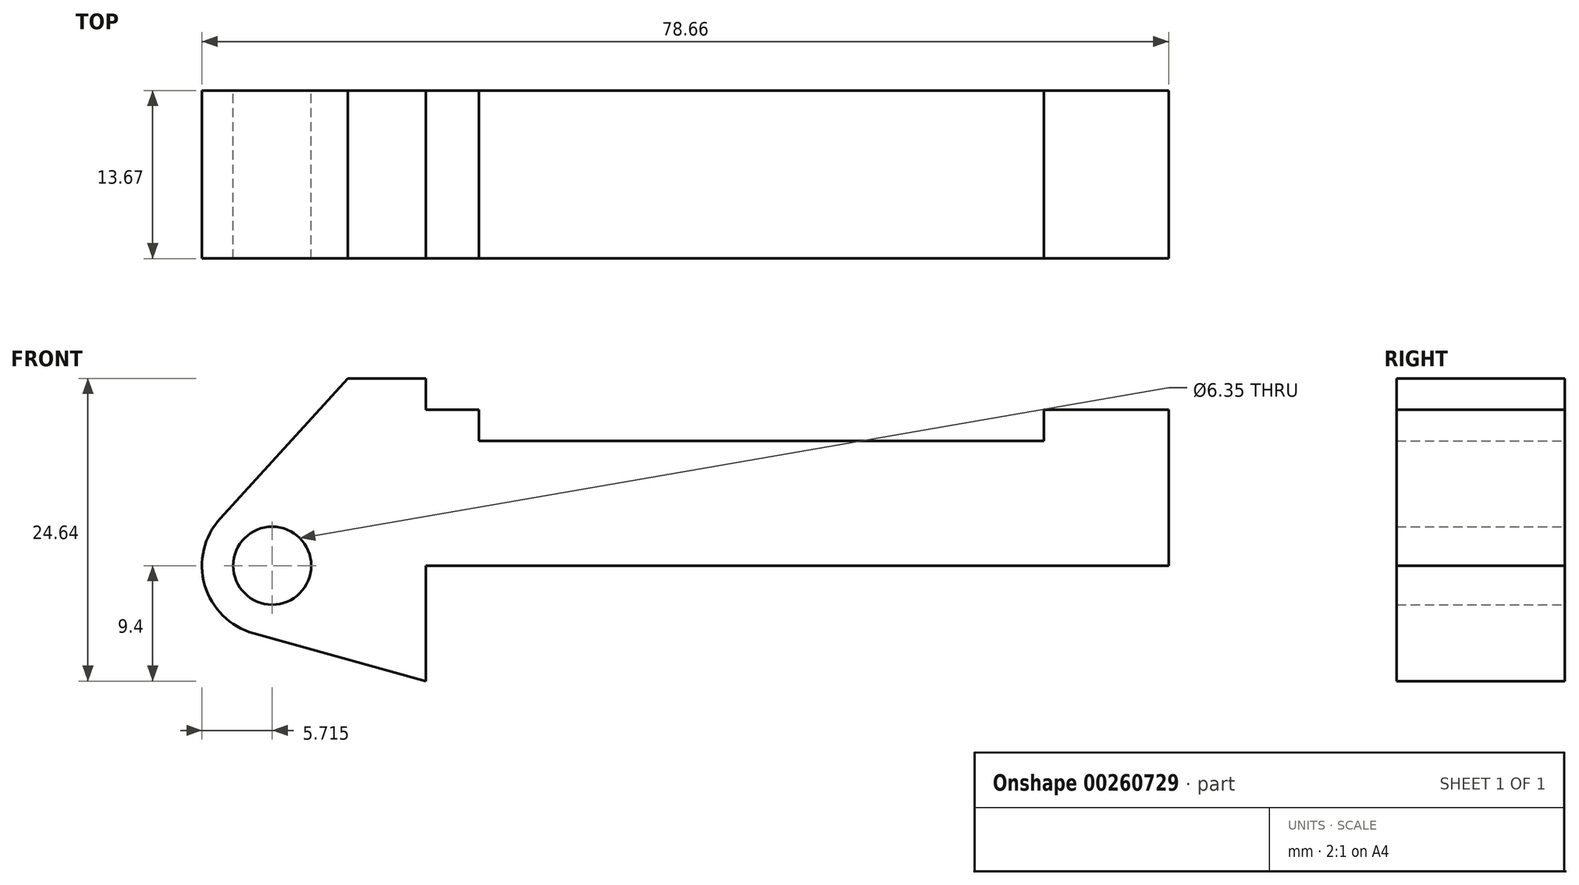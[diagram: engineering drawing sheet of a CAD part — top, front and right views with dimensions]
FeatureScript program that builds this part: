
annotation { "Feature Type Name" : "Feature", "Feature Type Description" : "" }
export const myFeature = defineFeature(function(context is Context, id is Id, definition is map)
    precondition{}
    {
        {
            var Q0;
            Q0=qCreatedBy(makeId("Front.planeOp"),FACE);
            var sketch = newSketch(context, id + "F0", { "sketchPlane" : qUnion([Q0])});
            skLineSegment(sketch, "E0", {"start": v(0, 0) * mm, "end": v(0, 12.7) * mm});
            skLineSegment(sketch, "E1", {"start": v(0, 12.7) * mm, "end": v(10.16, 12.7) * mm});
            skLineSegment(sketch, "E2", {"start": v(10.16, 12.7) * mm, "end": v(10.16, 10.16) * mm});
            skLineSegment(sketch, "E3", {"start": v(10.16, 10.16) * mm, "end": v(56.13, 10.16) * mm});
            skLineSegment(sketch, "E4", {"start": v(56.13, 10.16) * mm, "end": v(56.13, 12.7) * mm});
            skLineSegment(sketch, "E5", {"start": v(56.13, 12.7) * mm, "end": v(66.3, 12.7) * mm});
            skLineSegment(sketch, "E6", {"start": v(66.3, 12.7) * mm, "end": v(66.3, 0) * mm});
            skLineSegment(sketch, "E7", {"start": v(66.3, 0) * mm, "end": v(0, 0) * mm});
            skLineSegment(sketch, "E8", {"start": v(5.84, 15.24) * mm, "end": v(-0.5, 15.24) * mm});
            skLineSegment(sketch, "E9", {"start": v(-0.5, 15.24) * mm, "end": v(-10.88, 3.85) * mm});
            skLineSegment(sketch, "E10", {"start": v(0, 0) * mm, "end": v(-6.65, 0) * mm});
            skCircle(sketch, "E11", {"center": v(-6.65, 0) * mm, "radius": 5.72 * mm});
            skCircle(sketch, "E12", {"center": v(-6.65, 0) * mm, "radius": 3.18 * mm});
            skLineSegment(sketch, "E13", {"start": v(5.84, 15.24) * mm, "end": v(5.84, -9.4) * mm});
            skLineSegment(sketch, "E14", {"start": v(5.84, -9.4) * mm, "end": v(-8.18, -5.5) * mm});
            skSolve(sketch);
        }
        {
            var Q0;
            {var subQ4=sQuery(id+"F0.wireOp",EDGE,"E12");Q0=makeQuery(id+"F0.imprint","IMPRINT",FACE,{"disambiguationData":[TD([[makeQuery(id+"F0.imprint","IMPRINT",EDGE,{"derivedFrom":subQ4}),-1.0]])]});}
            var Q1;
            {var subQ3=sQuery(id+"F0.wireOp",EDGE,"E0");Q1=makeQuery(id+"F0.imprint","IMPRINT",FACE,{"disambiguationData":[TD([[makeQuery(id+"F0.imprint","IMPRINT",EDGE,{"derivedFrom":subQ3}),1.0]])]});}
            var Q2;
            Q2 = qSketchRegion(id + "F0", true);
            extrude(context, id + "F1", {"entities" : qUnion([Q0, Q1, Q2]), "depth" : 13.67 * mm});
        }
    });
